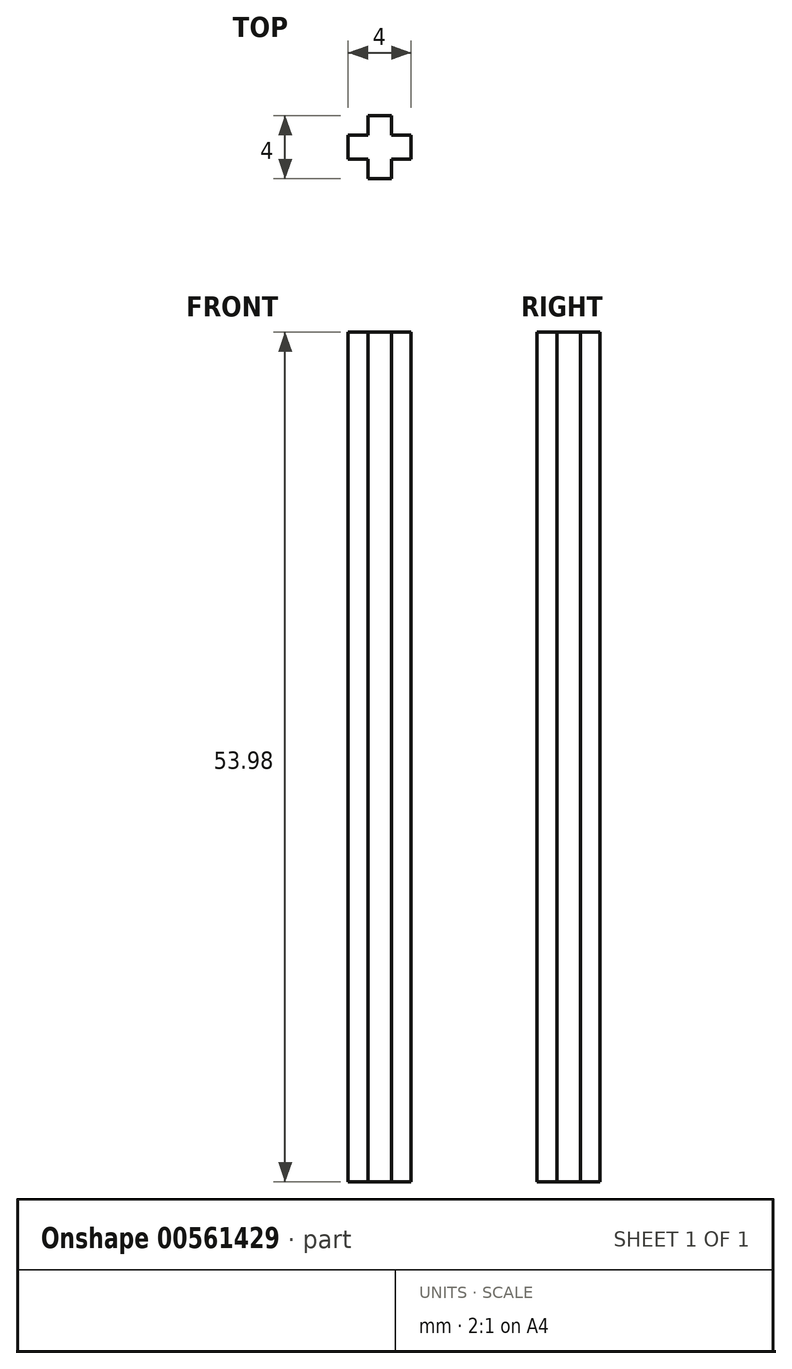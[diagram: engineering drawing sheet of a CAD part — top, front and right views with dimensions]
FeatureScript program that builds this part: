
annotation { "Feature Type Name" : "Feature", "Feature Type Description" : "" }
export const myFeature = defineFeature(function(context is Context, id is Id, definition is map)
    precondition{}
    {
        {
            var Q0;
            Q0=qCreatedBy(makeId("Top.planeOp"),FACE);
            var sketch = newSketch(context, id + "F0", { "sketchPlane" : qUnion([Q0])});
            skLineSegment(sketch, "E0", {"start": v(0, 2) * mm, "end": v(-0.75, 2) * mm});
            skLineSegment(sketch, "E1", {"start": v(0, 2) * mm, "end": v(0.75, 2) * mm});
            skLineSegment(sketch, "E2", {"start": v(-2, 0) * mm, "end": v(-2, 0.75) * mm});
            skLineSegment(sketch, "E3", {"start": v(-2, 0) * mm, "end": v(-2, -0.75) * mm});
            skLineSegment(sketch, "E4", {"start": v(0, -2) * mm, "end": v(-0.75, -2) * mm});
            skLineSegment(sketch, "E5", {"start": v(-0.75, -2) * mm, "end": v(0, -2) * mm});
            skLineSegment(sketch, "E6", {"start": v(0, -2) * mm, "end": v(0.75, -2) * mm});
            skLineSegment(sketch, "E7", {"start": v(2, 0.75) * mm, "end": v(2, 0) * mm});
            skLineSegment(sketch, "E8", {"start": v(2, 0) * mm, "end": v(2, -0.75) * mm});
            skLineSegment(sketch, "E9", {"start": v(-0.75, 2) * mm, "end": v(-0.75, 0.75) * mm});
            skLineSegment(sketch, "E10", {"start": v(0.75, 2) * mm, "end": v(0.75, 0.75) * mm});
            skLineSegment(sketch, "E11", {"start": v(2, 0.75) * mm, "end": v(0.75, 0.75) * mm});
            skLineSegment(sketch, "E12", {"start": v(-2, -0.75) * mm, "end": v(-0.75, -0.75) * mm});
            skLineSegment(sketch, "E13.trimOffspring", {"start": v(-0.75, 0.75) * mm, "end": v(-2, 0.75) * mm});
            skLineSegment(sketch, "E14.trimOffspring", {"start": v(0.75, -0.75) * mm, "end": v(2, -0.75) * mm});
            skLineSegment(sketch, "E15.trimOffspring", {"start": v(-0.75, -0.75) * mm, "end": v(-0.75, -2) * mm});
            skLineSegment(sketch, "E16.trimOffspring", {"start": v(0.75, -0.75) * mm, "end": v(0.75, -2) * mm});
            skSolve(sketch);
        }
        {
            var Q0;
            Q0=makeQuery(id+"F0.imprint","IMPRINT",FACE,{"disambiguationData":[TD([[makeQuery(id+"F0.imprint","IMPRINT",EDGE,{"derivedFrom":sQuery(id+"F0.wireOp",EDGE,"E0")}),1.0]])]});
            extrude(context, id + "F1", {"entities" : qUnion([Q0]), "depth" : 53.97 * mm, "offsetDistance" : 25.4 * mm});
        }
    });
